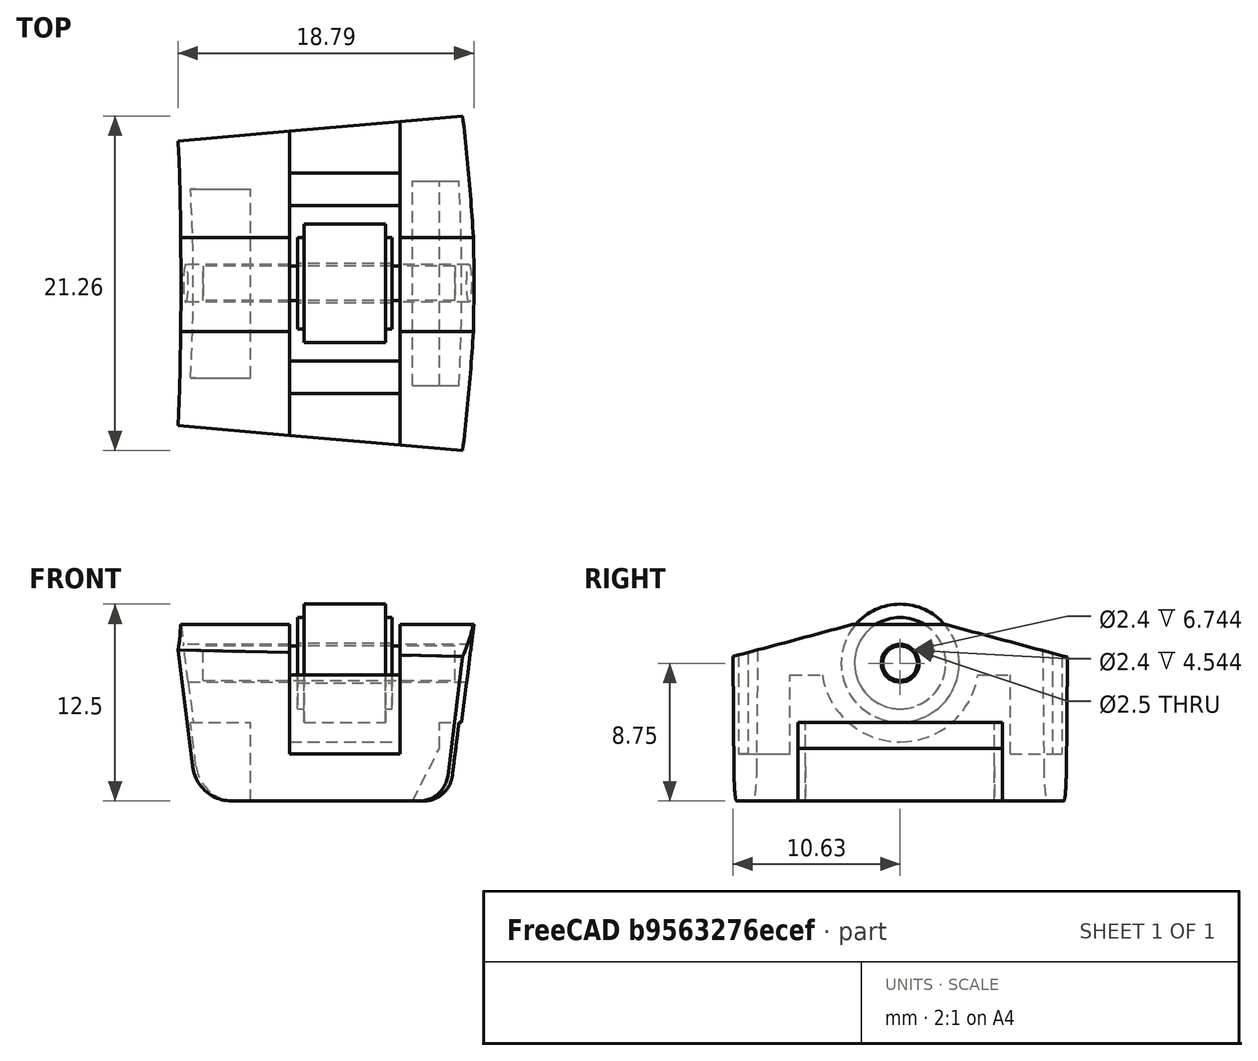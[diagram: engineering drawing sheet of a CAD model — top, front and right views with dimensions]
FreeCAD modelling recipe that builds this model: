
FCSTD DOCUMENT  (FreeCAD 0.20R29603 (Git))
Label: Roller Holder
License: All rights reserved
LicenseURL: http://en.wikipedia.org/wiki/All_rights_reserved
objects: Part::Cut×13, Part::Box×9, Part::Cylinder×6, Part::Fuse×2, Sketcher::SketchObject×1, Part::Revolution×1
note: 32 computed .brp shape members not serialized (recipe doc carries the construction recipe); baked Part::Feature solids carry a one-line shape summary decoded from their .brp

FEATURE [Sketcher::SketchObject] Sketch
  FullyConstrained = false
  Placement = pos=(0,0,0) rot=(1,0,0;1.5708rad)
  sketch-geometry (10):
    g0: LineSegment StartX=122.2 StartY=11.2 StartZ=0 EndX=121 EndY=1.6 EndZ=0
    g1: LineSegment StartX=107.22 StartY=4e-16 StartZ=0 EndX=119.188 EndY=4e-16 EndZ=0
    g2: LineSegment StartX=103.6 StartY=11.2 StartZ=0 EndX=104.725 EndY=2.20243 EndZ=0
    g3: LineSegment StartX=103.6 StartY=11.2 StartZ=0 EndX=122.2 EndY=11.2 EndZ=0
    g4: GeomPoint X=122.2 Y=11.2 Z=0
    g5: GeomPoint X=103.6 Y=11.2 Z=0
    g6: GeomPoint X=105 Y=0 Z=0
    g7: GeomPoint X=120.8 Y=0 Z=0
    g8: ArcOfCircle CenterX=119.188 CenterY=1.82656 CenterZ=0 NormalX=0 NormalY=0 NormalZ=1 AngleXU=0 Radius=1.82656 StartAngle=4.71239 EndAngle=6.15883
    g9: ArcOfCircle CenterX=107.22 CenterY=2.51429 CenterZ=0 NormalX=0 NormalY=0 NormalZ=1 AngleXU=0 Radius=2.51429 StartAngle=3.26595 EndAngle=4.71239
  constraints (8):
    c: Horizontal(g1)
    c: Horizontal(g3)
    c: Coincident(g4,g0)
    c: Coincident(g5,g2)
    c: Tangent(g0,g8) = 1.5708
    c: Tangent(g1,g8) = -1.5708
    c: Tangent(g2,g9) = -1.5708
    c: Tangent(g1,g9) = -1.5708
FEATURE [Part::Revolution] Revolve
  Angle = 10
  Axis = (0,0,1)
  Base = (0,0,0)
  FaceMakerClass = Part::FaceMakerBullseye
  Solid = true
  Source = -> Sketch
  Symmetric = true
FEATURE [Part::Cylinder] Cylinder  label="roller"
  Angle = 360
  AttacherType = Attacher::AttachEngine3D
  FirstAngle = 0
  Height = 6
  Placement = pos=(0,0,-3) rot=(0,0,1;0rad)
  Radius = 2.9
  SecondAngle = 0
FEATURE [Part::Cylinder] Cylinder001  label="rubber"
  Angle = 360
  AttacherType = Attacher::AttachEngine3D
  FirstAngle = 0
  Height = 5.2
  Placement = pos=(0,0,-2.6) rot=(0,0,1;0rad)
  Radius = 3.75
  SecondAngle = 0
FEATURE [Part::Cylinder] Cylinder002  label="Hole"
  Angle = 360
  AttacherType = Attacher::AttachEngine3D
  FirstAngle = 0
  Height = 6
  Placement = pos=(0,0,-3) rot=(0,0,1;0rad)
  Radius = 1.25
  SecondAngle = 0
FEATURE [Part::Fuse] Fusion  label="Roller"
  Base = -> Cylinder
  Tool = -> Cylinder001
FEATURE [Part::Cut] Cut  label="Roller001"
  Base = -> Fusion
  Placement = pos=(114,0,8.75) rot=(0,1,0;1.5708rad)
  Tool = -> Cylinder002
FEATURE [Part::Cylinder] Cylinder003  label="hole2"
  Angle = 360
  AttacherType = Attacher::AttachEngine3D
  FirstAngle = 0
  Height = 7
  Placement = pos=(110.5,0,8.75) rot=(0,1,0;1.5708rad)
  Radius = 5
  SecondAngle = 0
FEATURE [Part::Cut] Cut001
  Base = -> Revolve
  Tool = -> Cylinder003
FEATURE [Part::Box] Box  label="Куб"
  AttacherType = Attacher::AttachEngine3D
  Height = 3
  Length = 7
  Placement = pos=(110.5,-5,8.75) rot=(0,0,1;0rad)
  Width = 10
FEATURE [Part::Cut] Cut002
  Base = -> Cut001
  Tool = -> Box
FEATURE [Part::Cylinder] Cylinder004  label="HOLE3"
  Angle = 360
  AttacherType = Attacher::AttachEngine3D
  FirstAngle = 0
  Height = 20
  Placement = pos=(103,0,8.75) rot=(0,1,0;1.5708rad)
  Radius = 1.2
  SecondAngle = 0
FEATURE [Part::Cut] Cut003  label="Base"
  Base = -> Cut002
  Tool = -> Cylinder004
FEATURE [Part::Cylinder] Cylinder005  label="Spindel"
  Angle = 360
  AttacherType = Attacher::AttachEngine3D
  FirstAngle = 0
  Height = 16
  Placement = pos=(105,0,8.75) rot=(0,1,0;1.5708rad)
  Radius = 1.1
  SecondAngle = 0
FEATURE [Part::Box] Box001  label="Куб001"
  AttacherType = Attacher::AttachEngine3D
  Height = 5
  Length = 6
  Placement = pos=(102,-6,0) rot=(0,0,1;0rad)
  Width = 12
FEATURE [Part::Box] Box002  label="Куб002"
  AttacherType = Attacher::AttachEngine3D
  Height = 5
  Length = 6
  Placement = pos=(120,-6.5,0) rot=(0,0,1;0rad)
  Width = 13
FEATURE [Part::Cut] Cut004
  Base = -> Cut003
  Tool = -> Box001
FEATURE [Part::Cut] Cut006
  Base = -> Cut004
  Tool = -> Box002
FEATURE [Part::Box] Box003  label="Куб003"
  AttacherType = Attacher::AttachEngine3D
  Height = 4
  Length = 25
  Placement = pos=(100,-15,8) rot=(1,0,0;0.261799rad)
  Width = 30
FEATURE [Part::Box] Box004  label="Куб004"
  AttacherType = Attacher::AttachEngine3D
  Height = 4
  Length = 25
  Placement = pos=(100,-15,16) rot=(1,0,0;-0.261799rad)
  Width = 30
FEATURE [Part::Cut] Cut005
  Base = -> Cut004
  Tool = -> Box002
FEATURE [Part::Fuse] Fusion001
  Base = -> Cut005
  Tool = -> Cut006
FEATURE [Part::Cut] Cut007
  Base = -> Fusion001
  Tool = -> Box003
FEATURE [Part::Cut] Cut008
  Base = -> Cut007
  Tool = -> Box004
FEATURE [Part::Box] Box005  label="Куб005"
  AttacherType = Attacher::AttachEngine3D
  Height = 9
  Length = 7
  Placement = pos=(110.5,-15,8) rot=(0,0,1;0rad)
  Width = 30
FEATURE [Part::Cut] Cut009
  Base = -> Cut008
  Tool = -> Box005
FEATURE [Part::Box] Box006  label="Куб006"
  AttacherType = Attacher::AttachEngine3D
  Height = 11
  Length = 7
  Placement = pos=(110.5,7,3) rot=(0,0,1;0rad)
  Width = 5
FEATURE [Part::Box] Box007  label="Куб007"
  AttacherType = Attacher::AttachEngine3D
  Height = 11
  Length = 7
  Placement = pos=(110.5,-12,3) rot=(0,0,1;0rad)
  Width = 5
FEATURE [Part::Cut] Cut010
  Base = -> Cut009
  Tool = -> Box006
FEATURE [Part::Cut] Cut011
  Base = -> Cut010
  Tool = -> Box007
FEATURE [Part::Box] Box008  label="Куб008"
  AttacherType = Attacher::AttachEngine3D
  Height = 5
  Length = 2
  Placement = pos=(118.3,-6.5,0) rot=(0,1,0;0.471239rad)
  Width = 13
FEATURE [Part::Cut] Cut012
  Base = -> Cut011
  Tool = -> Box008
